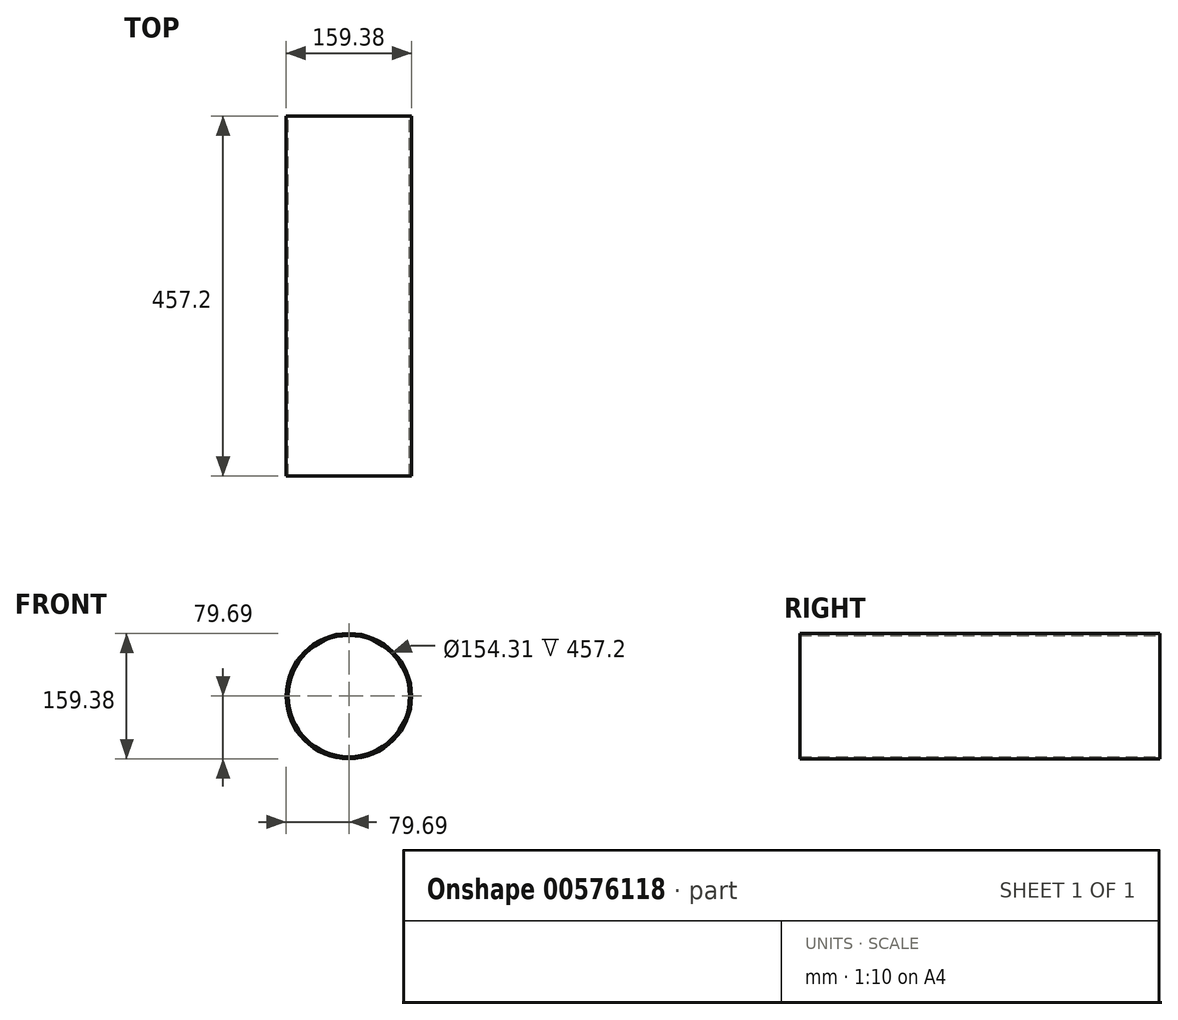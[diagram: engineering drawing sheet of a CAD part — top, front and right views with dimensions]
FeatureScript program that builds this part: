
annotation { "Feature Type Name" : "Feature", "Feature Type Description" : "" }
export const myFeature = defineFeature(function(context is Context, id is Id, definition is map)
    precondition{}
    {
        {
            var Q0;
            Q0=qCreatedBy(makeId("Front.planeOp"),FACE);
            var sketch = newSketch(context, id + "F0", { "sketchPlane" : qUnion([Q0])});
            skCircle(sketch, "E0", {"center": v(0, 0) * mm, "radius": 77.15 * mm});
            skCircle(sketch, "E1", {"center": v(0, 0) * mm, "radius": 79.7 * mm});
            skSolve(sketch);
        }
        {
            var Q0;
            Q0=qSketchRegion(id+"F0",true);
            extrude(context, id + "F1", {"entities" : qUnion([Q0]), "endBound" : BoundingType.SYMMETRIC, "depth" : 457.2 * mm, "offsetDistance" : 25.4 * mm});
        }
    });
